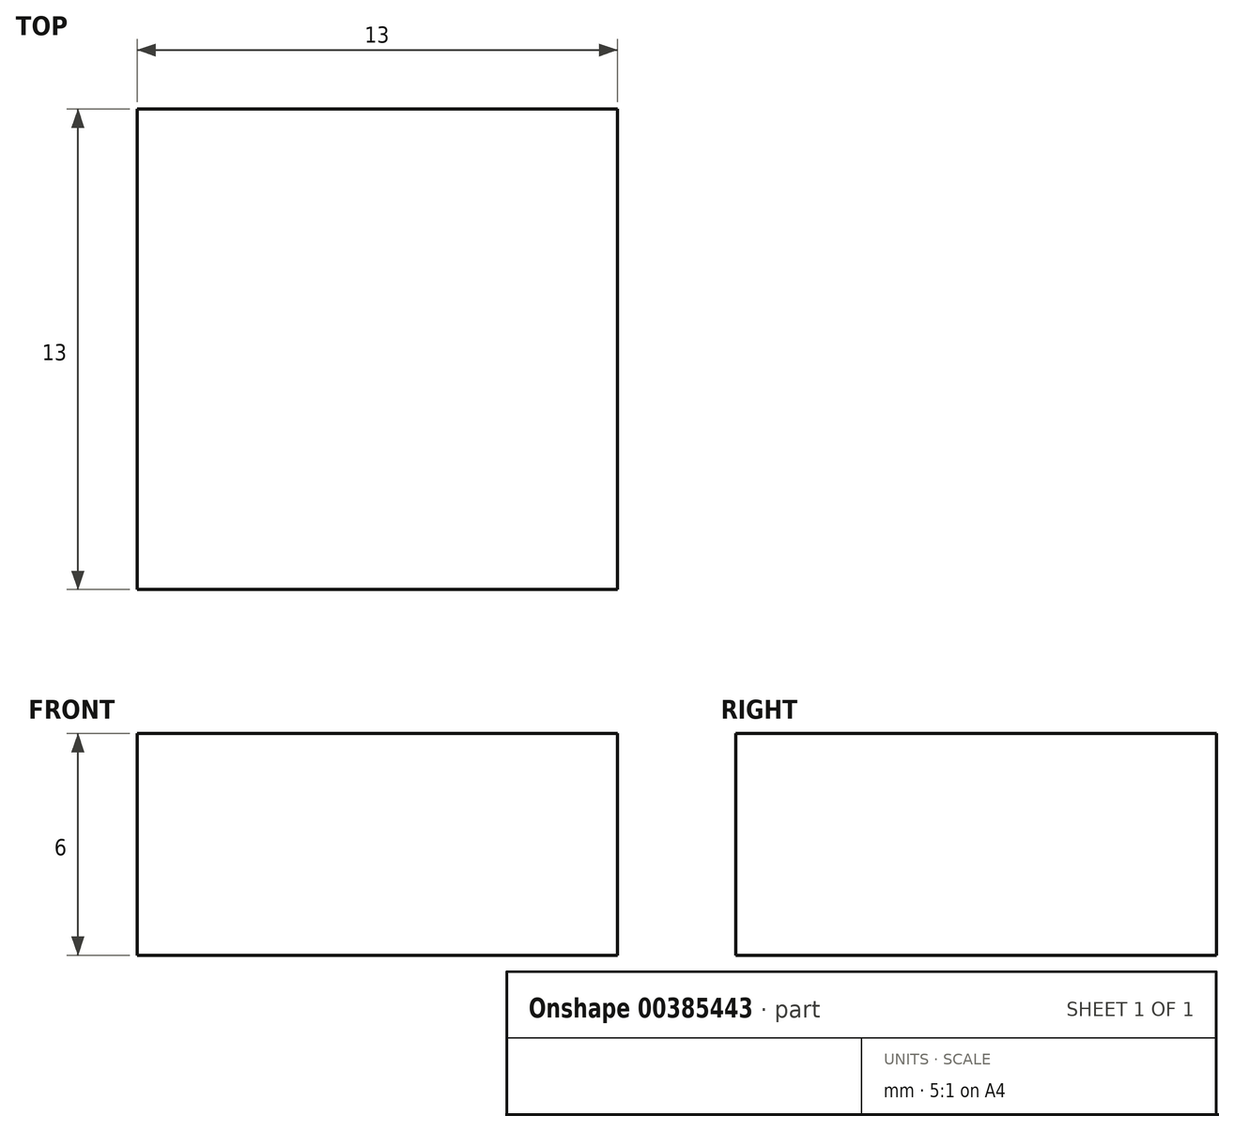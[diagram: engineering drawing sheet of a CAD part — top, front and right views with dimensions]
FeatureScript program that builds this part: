
annotation { "Feature Type Name" : "Feature", "Feature Type Description" : "" }
export const myFeature = defineFeature(function(context is Context, id is Id, definition is map)
    precondition{}
    {
        {
            var Q0;
            Q0=qCreatedBy(makeId("Top.planeOp"),FACE);
            var sketch = newSketch(context, id + "F0", { "sketchPlane" : qUnion([Q0])});
            skLineSegment(sketch, "E0.bottom", {"start": v(6.5, -6.5) * mm, "end": v(-6.5, -6.5) * mm});
            skLineSegment(sketch, "E0.top", {"start": v(6.5, 6.5) * mm, "end": v(-6.5, 6.5) * mm});
            skLineSegment(sketch, "E0.left", {"start": v(6.5, -6.5) * mm, "end": v(6.5, 6.5) * mm});
            skLineSegment(sketch, "E0.right", {"start": v(-6.5, -6.5) * mm, "end": v(-6.5, 6.5) * mm});
            skPoint(sketch, "E0.middle", {"position": v(0, 0) * mm});
            skSolve(sketch);
        }
        {
            var Q0;
            Q0=makeQuery(id+"F0.imprint","IMPRINT",FACE,{"disambiguationData":[TD([[makeQuery(id+"F0.imprint","IMPRINT",EDGE,{"derivedFrom":sQuery(id+"F0.wireOp",EDGE,"E0.bottom")}),-1.0]])]});
            extrude(context, id + "F1", {"entities" : qUnion([Q0]), "depth" : 6 * mm});
        }
    });
